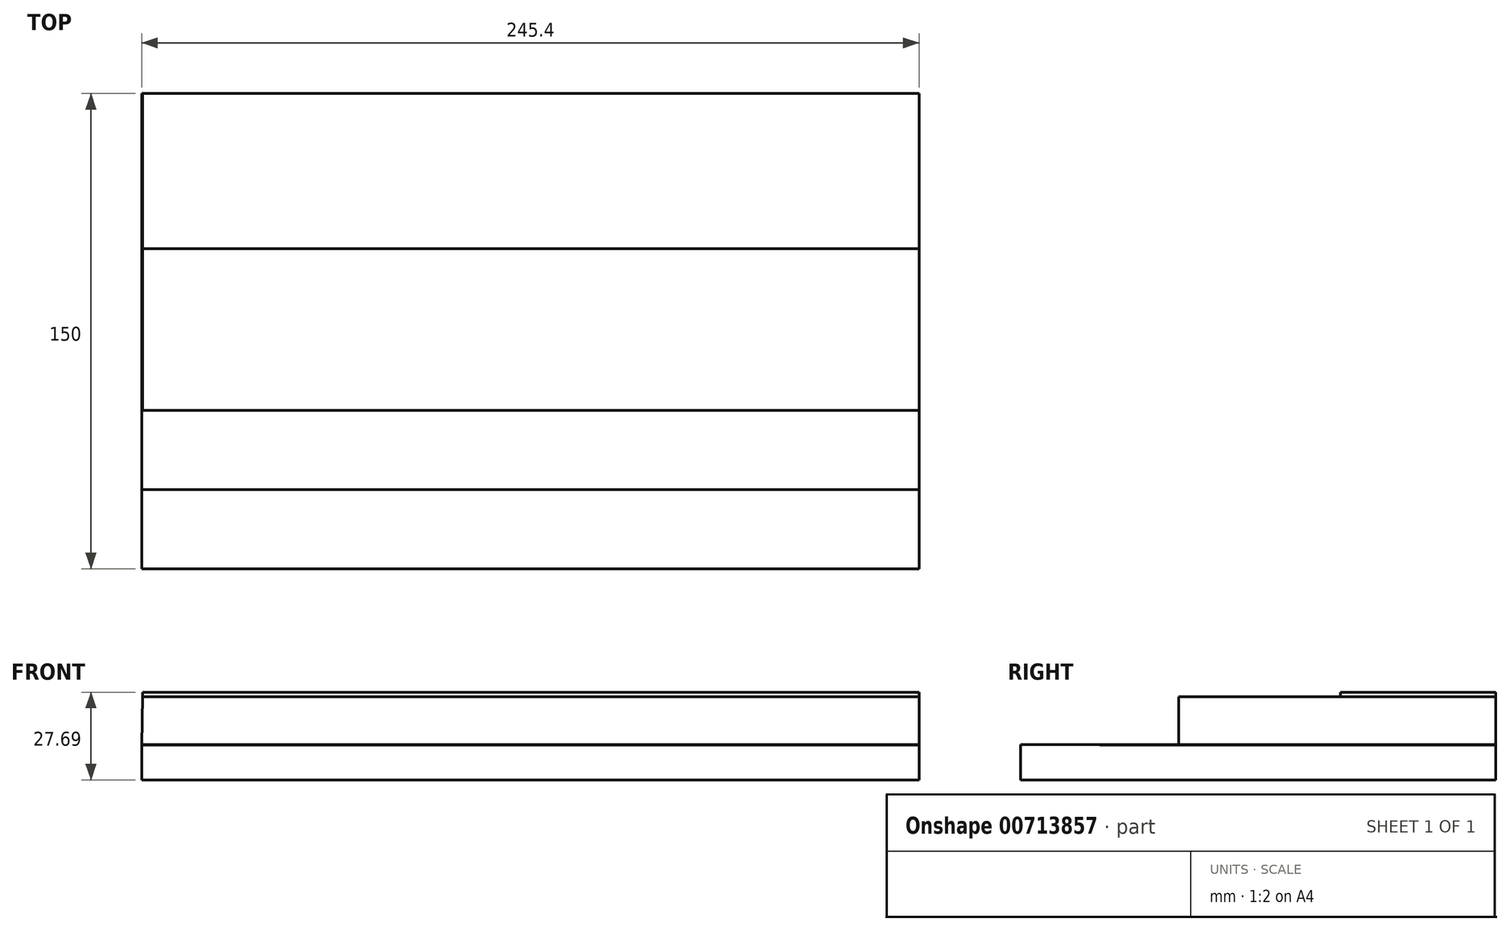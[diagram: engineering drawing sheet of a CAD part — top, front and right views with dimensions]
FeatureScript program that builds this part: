
annotation { "Feature Type Name" : "Feature", "Feature Type Description" : "" }
export const myFeature = defineFeature(function(context is Context, id is Id, definition is map)
    precondition{}
    {
        {
            var Q0;
            Q0=qCreatedBy(makeId("Front.planeOp"),FACE);
            var sketch = newSketch(context, id + "F0", { "sketchPlane" : qUnion([Q0])});
            skLineSegment(sketch, "E0", {"start": v(-43.05, 16) * mm, "end": v(-21.76, 16) * mm});
            skLineSegment(sketch, "E1", {"start": v(20.95, 16) * mm, "end": v(42.24, 16) * mm});
            skLineSegment(sketch, "E2", {"start": v(84.95, 16) * mm, "end": v(106.24, 16) * mm});
            skLineSegment(sketch, "E3", {"start": v(148.95, 16) * mm, "end": v(170.24, 16) * mm});
            skLineSegment(sketch, "E4", {"start": v(-75.16, 16) * mm, "end": v(170.24, 16) * mm});
            skLineSegment(sketch, "E5", {"start": v(170.24, 31) * mm, "end": v(-74.91, 31) * mm});
            skLineSegment(sketch, "E6", {"start": v(-74.91, 31) * mm, "end": v(-75.16, 16) * mm});
            skLineSegment(sketch, "E7", {"start": v(170.24, 31) * mm, "end": v(170.24, 16) * mm});
            skLineSegment(sketch, "E8", {"start": v(-74.91, 31) * mm, "end": v(-74.91, 32.5) * mm});
            skLineSegment(sketch, "E9", {"start": v(-74.91, 32.5) * mm, "end": v(170.2, 32.5) * mm});
            skLineSegment(sketch, "E10", {"start": v(170.2, 32.5) * mm, "end": v(170.24, 31) * mm});
            skLineSegment(sketch, "E11", {"start": v(-75.16, 16) * mm, "end": v(-75.16, 15.8) * mm});
            skLineSegment(sketch, "E12", {"start": v(-75.16, 15.8) * mm, "end": v(170.24, 15.8) * mm});
            skLineSegment(sketch, "E13", {"start": v(170.24, 15.8) * mm, "end": v(170.24, 16) * mm});
            skLineSegment(sketch, "E14", {"start": v(-75.16, 15.8) * mm, "end": v(-75.16, 4.81) * mm});
            skLineSegment(sketch, "E15", {"start": v(-75.16, 4.81) * mm, "end": v(170.24, 4.81) * mm});
            skLineSegment(sketch, "E16", {"start": v(170.24, 4.81) * mm, "end": v(170.24, 16) * mm});
            skSolve(sketch);
        }
        {
            var Q0;
            {var subQ6=sQuery(id+"F0.wireOp",EDGE,"E11");Q0=makeQuery(id+"F0.imprint","IMPRINT",FACE,{"disambiguationData":[TD([[makeQuery(id+"F0.imprint","IMPRINT",EDGE,{"derivedFrom":subQ6}),1.0]])]});}
            extrude(context, id + "F1", {"entities" : qUnion([Q0]), "depth" : 125 * mm});
        }
        {
            var Q0;
            Q0=makeQuery(id+"F0.imprint","IMPRINT",FACE,{"disambiguationData":[TD([[makeQuery(id+"F0.imprint","IMPRINT",EDGE,{"derivedFrom":sQuery(id+"F0.wireOp",EDGE,"E5")}),1.0]])]});
            extrude(context, id + "F2", {"entities" : qUnion([Q0]), "depth" : 100 * mm});
        }
        {
            var Q0;
            Q0=makeQuery(id+"F0.imprint","IMPRINT",FACE,{"disambiguationData":[TD([[makeQuery(id+"F0.imprint","IMPRINT",EDGE,{"derivedFrom":sQuery(id+"F0.wireOp",EDGE,"E5")}),-1.0]])]});
            extrude(context, id + "F3", {"entities" : qUnion([Q0]), "depth" : 49 * mm});
        }
        {
            var Q0;
            Q0=makeQuery(id+"F0.imprint","IMPRINT",FACE,{"disambiguationData":[TD([[makeQuery(id+"F0.imprint","IMPRINT",EDGE,{"derivedFrom":sQuery(id+"F0.wireOp",EDGE,"E12")}),-1.0]])]});
            extrude(context, id + "F4", {"entities" : qUnion([Q0]), "depth" : 150 * mm});
        }
    });
